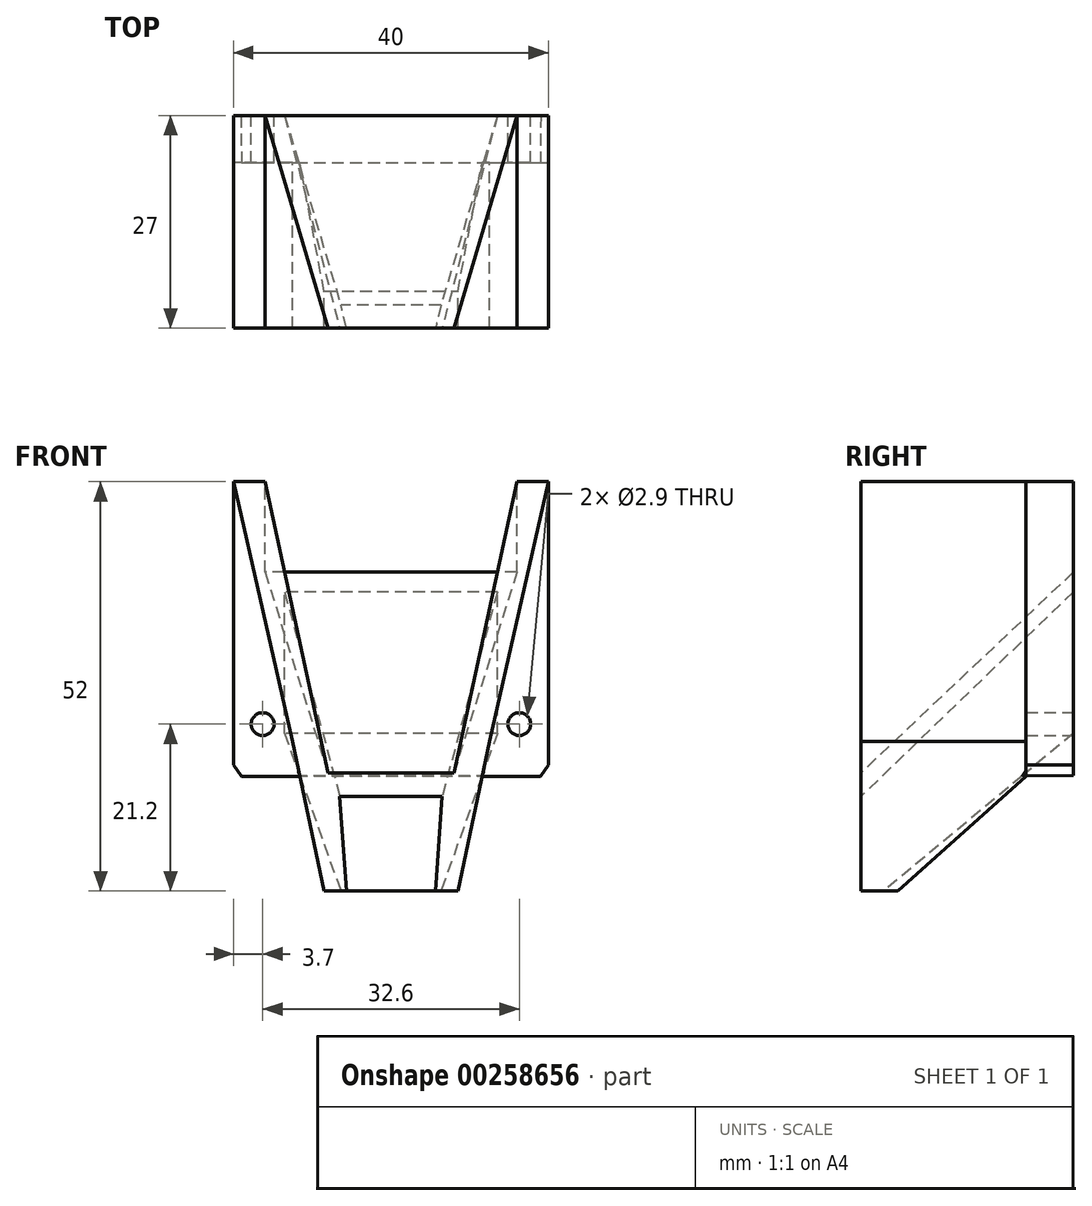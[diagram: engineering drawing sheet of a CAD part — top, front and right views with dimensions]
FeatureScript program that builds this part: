
annotation { "Feature Type Name" : "Feature", "Feature Type Description" : "" }
export const myFeature = defineFeature(function(context is Context, id is Id, definition is map)
    precondition{}
    {
        {
            var Q0;
            Q0=qCreatedBy(makeId("Front.planeOp"),FACE);
            var sketch = newSketch(context, id + "F0", { "sketchPlane" : qUnion([Q0])});
            skLineSegment(sketch, "E0.bottom", {"start": v(20, -26) * mm, "end": v(-20, -26) * mm});
            skLineSegment(sketch, "E0.top", {"start": v(20, 26) * mm, "end": v(-20, 26) * mm});
            skLineSegment(sketch, "E0.left", {"start": v(20, -26) * mm, "end": v(20, 26) * mm});
            skLineSegment(sketch, "E0.right", {"start": v(-20, -26) * mm, "end": v(-20, 26) * mm});
            skPoint(sketch, "E0.middle", {"position": v(0, 0) * mm});
            skCircle(sketch, "E1", {"center": v(-16.3, -4.8) * mm, "radius": 1.45 * mm});
            skCircle(sketch, "E2.MirrorC", {"center": v(16.3, -4.8) * mm, "radius": 1.45 * mm});
            skPoint(sketch, "E3", {"position": v(-8.5, -26) * mm});
            skPoint(sketch, "E4", {"position": v(-20, -10) * mm});
            skLineSegment(sketch, "E5", {"start": v(-8.5, -26) * mm, "end": v(-20, -10) * mm});
            skLineSegment(sketch, "E6.MirrorCS", {"start": v(8.5, -26) * mm, "end": v(20, -10) * mm});
            skSolve(sketch);
        }
        {
            var Q0;
            {var subQ1=sQuery(id+"F0.wireOp",EDGE,"E0.top");Q0=makeQuery(id+"F0.imprint","IMPRINT",FACE,{"disambiguationData":[TD([[makeQuery(id+"F0.imprint","IMPRINT",EDGE,{"derivedFrom":subQ1}),1.0]])]});}
            extrude(context, id + "F1", {"entities" : qUnion([Q0]), "depth" : 27 * mm});
        }
        {
            var Q0;
            Q0=qCreatedBy(makeId("Front.planeOp"),FACE);
            var sketch = newSketch(context, id + "F2", { "sketchPlane" : qUnion([Q0])});
            skLineSegment(sketch, "E7.right", {"start": v(26.5, 0) * mm, "end": v(26.5, -25) * mm});
            skPoint(sketch, "E7.middle", {"position": v(19.5, -12.5) * mm});
            skLineSegment(sketch, "E8.MirrorCS", {"start": v(-8.5, -25.1) * mm, "end": v(-8.52, -25) * mm});
            skLineSegment(sketch, "E9.MirrorCS", {"start": v(-8.5, -25) * mm, "end": v(-8.52, -25) * mm});
            skLineSegment(sketch, "E10", {"start": v(12.5, -7) * mm, "end": v(8.5, -26) * mm});
            skLineSegment(sketch, "E11", {"start": v(26.5, -25) * mm, "end": v(8.5, -26) * mm});
            skLineSegment(sketch, "E12", {"start": v(12.5, -7) * mm, "end": v(20, 26) * mm});
            skLineSegment(sketch, "E13", {"start": v(20, 26) * mm, "end": v(26.5, 0) * mm});
            skPoint(sketch, "E14.MirrorCS.end.orphan", {"position": v(-8.5, -26) * mm});
            skLineSegment(sketch, "E15.MirrorCS", {"start": v(-12.5, -7) * mm, "end": v(-20, 26) * mm});
            skLineSegment(sketch, "E16.MirrorCS", {"start": v(-12.5, -7) * mm, "end": v(-8.5, -26) * mm});
            skLineSegment(sketch, "E17.MirrorCS", {"start": v(-26.5, -25) * mm, "end": v(-8.5, -26) * mm});
            skLineSegment(sketch, "E18.MirrorCS", {"start": v(-26.5, 0) * mm, "end": v(-26.5, -25) * mm});
            skLineSegment(sketch, "E19.MirrorCS", {"start": v(-20, 26) * mm, "end": v(-26.5, 0) * mm});
            skSolve(sketch);
        }
        {
            var Q0;
            Q0 = qSketchRegion(id + "F2", true);
            extrude(context, id + "F3", {"entities" : qUnion([Q0]), "operationType" : NewBodyOperationType.REMOVE, "depth" : 29 * mm, "hasSecondDirection" : true, "secondDirectionOppositeDirection" : false, "secondDirectionDepth" : 6 * mm});
        }
        {
            var Q0;
            Q0=qCreatedBy(makeId("Front.planeOp"),FACE);
            cPlane(context, id + "F4", {"entities" : qUnion([Q0]), "cplaneType" : CPlaneType.OFFSET, "offset" : 27 * mm, "width" : 150 * mm, "height" : 150 * mm});
        }
        {
            var Q0;
            Q0=qCreatedBy(id+"F4.planeOp",FACE);
            var sketch = newSketch(context, id + "F5", { "sketchPlane" : qUnion([Q0])});
            skLineSegment(sketch, "E20.top", {"start": v(6.5, -14) * mm, "end": v(-6.5, -14) * mm});
            skPoint(sketch, "E20.middle", {"position": v(0, -21.5) * mm});
            skLineSegment(sketch, "E21.top", {"start": v(16, 26) * mm, "end": v(-16, 26) * mm});
            skLineSegment(sketch, "E22", {"start": v(-8, -11) * mm, "end": v(8, -11) * mm});
            skLineSegment(sketch, "E23", {"start": v(-16, 26) * mm, "end": v(-8, -11) * mm});
            skLineSegment(sketch, "E24", {"start": v(8, -11) * mm, "end": v(16, 26) * mm});
            skLineSegment(sketch, "E25", {"start": v(-5.5, -28.4) * mm, "end": v(-6.5, -14) * mm});
            skLineSegment(sketch, "E26", {"start": v(5.5, -28.4) * mm, "end": v(6.5, -14) * mm});
            skLineSegment(sketch, "E27", {"start": v(-5.5, -28.4) * mm, "end": v(5.5, -28.4) * mm});
            skSolve(sketch);
        }
        {
            var Q0;
            Q0=qCreatedBy(makeId("Front.planeOp"),FACE);
            var sketch = newSketch(context, id + "F6", { "sketchPlane" : qUnion([Q0])});
            skLineSegment(sketch, "E28.bottom", {"start": v(13.5, -6) * mm, "end": v(-13.5, -6) * mm});
            skLineSegment(sketch, "E28.top", {"start": v(13.5, 12) * mm, "end": v(-13.5, 12) * mm});
            skLineSegment(sketch, "E28.left", {"start": v(13.5, -6) * mm, "end": v(13.5, 12) * mm});
            skLineSegment(sketch, "E28.right", {"start": v(-13.5, -6) * mm, "end": v(-13.5, 12) * mm});
            skPoint(sketch, "E28.middle", {"position": v(0, 3) * mm});
            skLineSegment(sketch, "E29.bottom", {"start": v(16, 14.5) * mm, "end": v(-16, 14.5) * mm});
            skLineSegment(sketch, "E29.top", {"start": v(16, 26) * mm, "end": v(-16, 26) * mm});
            skLineSegment(sketch, "E29.left", {"start": v(16, 14.5) * mm, "end": v(16, 26) * mm});
            skLineSegment(sketch, "E29.right", {"start": v(-16, 14.5) * mm, "end": v(-16, 26) * mm});
            skPoint(sketch, "E29.middle", {"position": v(0, 20.25) * mm});
            skSolve(sketch);
        }
        {
            var Q1;
            Q1=makeQuery(id+"F6.imprint","IMPRINT",FACE,{"disambiguationData":[TD([[makeQuery(id+"F6.imprint","IMPRINT",EDGE,{"derivedFrom":sQuery(id+"F6.wireOp",EDGE,"E29.bottom")}),-1.0]])]});
            var Q2;
            Q2=makeQuery(id+"F5.imprint","IMPRINT",FACE,{"disambiguationData":[TD([[makeQuery(id+"F5.imprint","IMPRINT",EDGE,{"derivedFrom":sQuery(id+"F5.wireOp",EDGE,"E21.top")}),1.0]])]});
            loft(context, id + "F7", {"operationType" : NewBodyOperationType.REMOVE, "sheetProfilesArray" : [{ "sheetProfileEntities" : qUnion([Q1]) }, { "sheetProfileEntities" : qUnion([Q2]) }]});
        }
        {
            var Q0;
            Q0=qCreatedBy(makeId("Right.planeOp"),FACE);
            var sketch = newSketch(context, id + "F8", { "sketchPlane" : qUnion([Q0])});
            skLineSegment(sketch, "E30", {"start": v(-27.2, -30.37) * mm, "end": v(-5.97, -11.4) * mm});
            skLineSegment(sketch, "E31", {"start": v(-5.97, -11.4) * mm, "end": v(2.92, -11.33) * mm});
            skLineSegment(sketch, "E32", {"start": v(2.92, -11.33) * mm, "end": v(3.78, -39.44) * mm});
            skLineSegment(sketch, "E33", {"start": v(3.78, -39.44) * mm, "end": v(-27.2, -30.37) * mm});
            skSolve(sketch);
        }
        {
            var Q0;
            Q0=makeQuery(id+"F8.imprint","IMPRINT",FACE,{"disambiguationData":[TD([[makeQuery(id+"F8.imprint","IMPRINT",EDGE,{"derivedFrom":sQuery(id+"F8.wireOp",EDGE,"E30")}),-1.0]])]});
            extrude(context, id + "F9", {"entities" : qUnion([Q0]), "operationType" : NewBodyOperationType.REMOVE, "oppositeDirection" : true, "depth" : 25 * mm, "hasSecondDirection" : true, "secondDirectionOppositeDirection" : false, "secondDirectionDepth" : 25 * mm});
        }
        {
            var Q1;
            Q1=makeQuery(id+"F6.imprint","IMPRINT",FACE,{"disambiguationData":[TD([[makeQuery(id+"F6.imprint","IMPRINT",EDGE,{"derivedFrom":sQuery(id+"F6.wireOp",EDGE,"E28.bottom")}),-1.0]])]});
            var Q2;
            Q2=makeQuery(id+"F5.imprint","IMPRINT",FACE,{"disambiguationData":[TD([[makeQuery(id+"F5.imprint","IMPRINT",EDGE,{"derivedFrom":sQuery(id+"F5.wireOp",EDGE,"E20.top")}),1.0]])]});
            loft(context, id + "F10", {"operationType" : NewBodyOperationType.REMOVE, "sheetProfilesArray" : [{ "sheetProfileEntities" : qUnion([Q1]) }, { "sheetProfileEntities" : qUnion([Q2]) }]});
        }
    });
